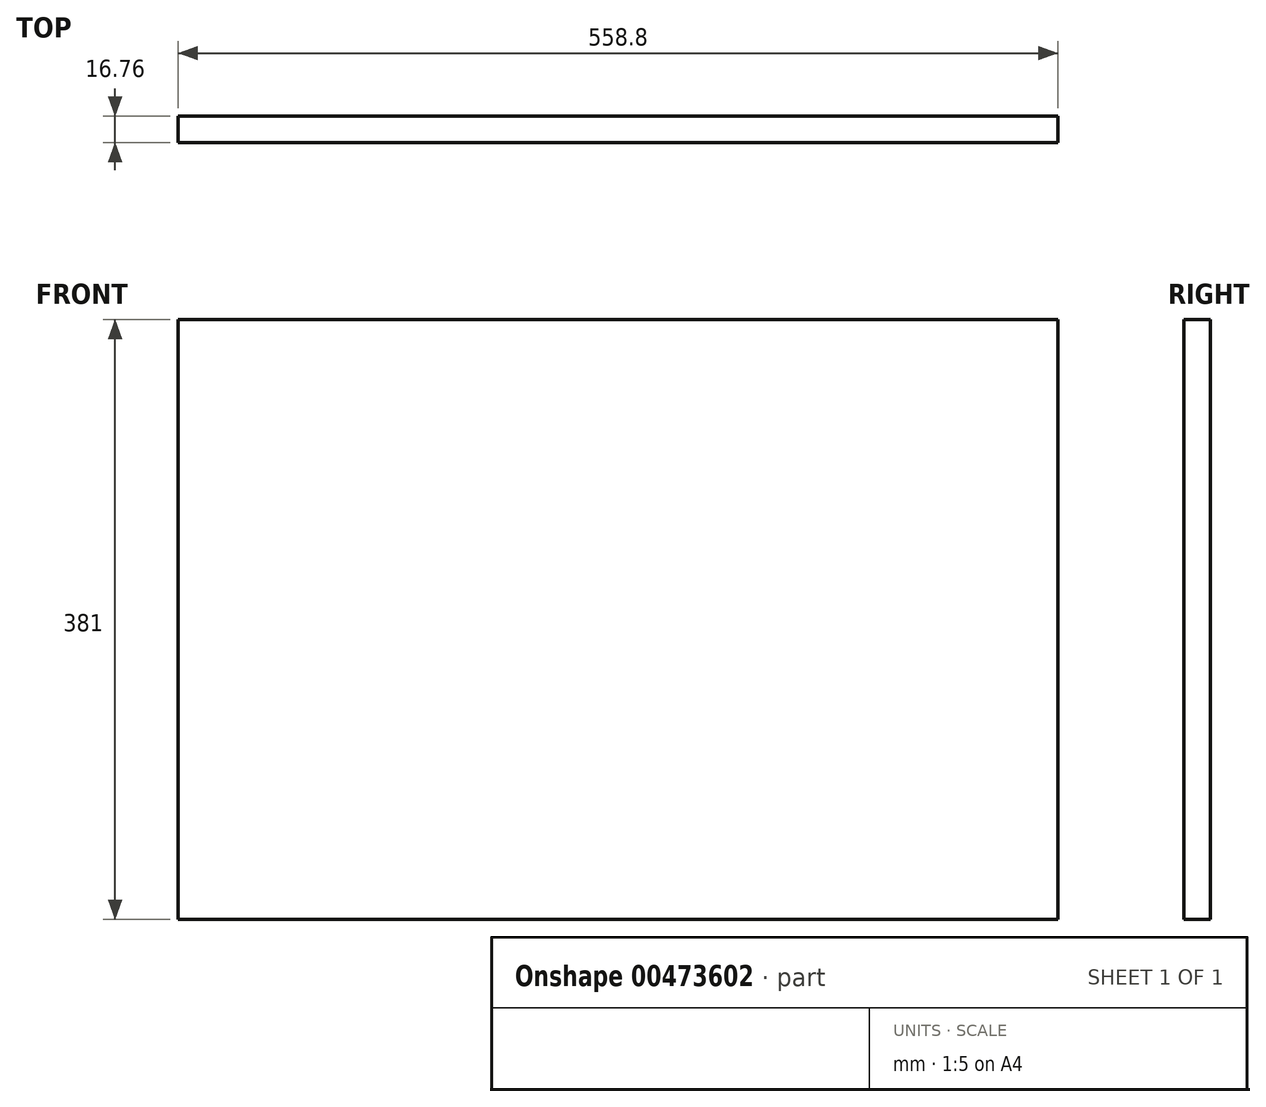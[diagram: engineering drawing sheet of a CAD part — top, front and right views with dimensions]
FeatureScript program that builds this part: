
annotation { "Feature Type Name" : "Feature", "Feature Type Description" : "" }
export const myFeature = defineFeature(function(context is Context, id is Id, definition is map)
    precondition{}
    {
        {
            var Q0;
            Q0=qCreatedBy(makeId("Front.planeOp"),FACE);
            var sketch = newSketch(context, id + "F0", { "sketchPlane" : qUnion([Q0])});
            skLineSegment(sketch, "E0.bottom", {"start": v(279.4, 190.5) * mm, "end": v(-279.4, 190.5) * mm});
            skLineSegment(sketch, "E0.top", {"start": v(279.4, -190.5) * mm, "end": v(-279.4, -190.5) * mm});
            skLineSegment(sketch, "E0.left", {"start": v(279.4, 190.5) * mm, "end": v(279.4, -190.5) * mm});
            skLineSegment(sketch, "E0.right", {"start": v(-279.4, 190.5) * mm, "end": v(-279.4, -190.5) * mm});
            skPoint(sketch, "E0.middle", {"position": v(0, 0) * mm});
            skSolve(sketch);
        }
        {
            var Q0;
            Q0=makeQuery(id+"F0.imprint","IMPRINT",FACE,{"disambiguationData":[TD([[makeQuery(id+"F0.imprint","IMPRINT",EDGE,{"derivedFrom":sQuery(id+"F0.wireOp",EDGE,"E0.bottom")}),1.0]])]});
            extrude(context, id + "F1", {"entities" : qUnion([Q0]), "depth" : 16.76 * mm});
        }
    });
